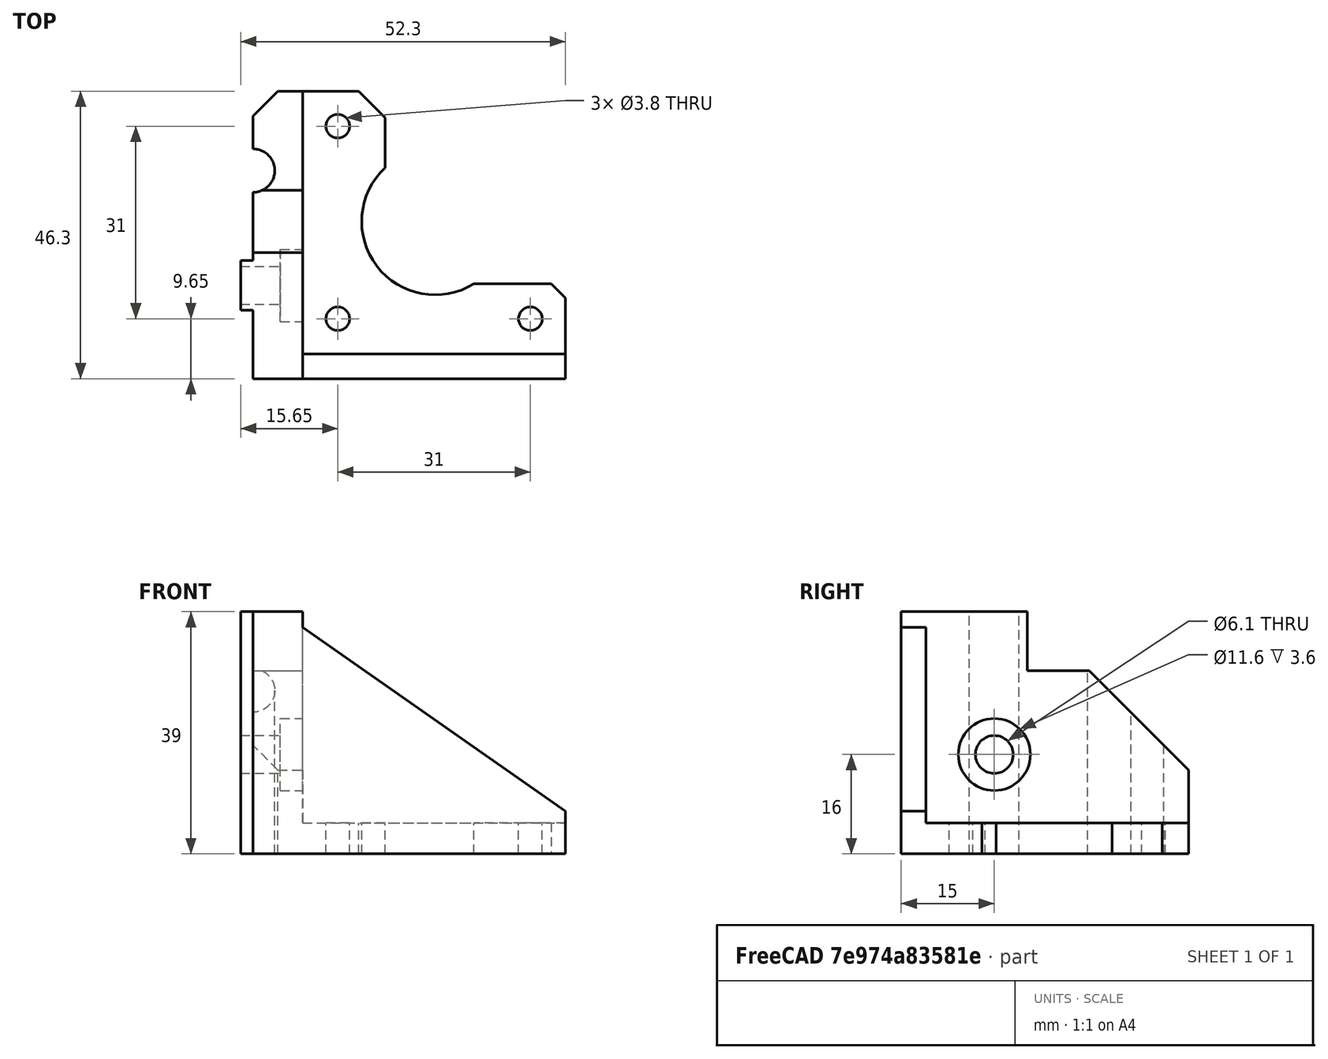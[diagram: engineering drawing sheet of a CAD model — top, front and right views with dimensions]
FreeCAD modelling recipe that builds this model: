
FCSTD DOCUMENT  (FreeCAD 0.19R)
Label: y-motor
License: All rights reserved
LicenseURL: http://en.wikipedia.org/wiki/All_rights_reserved
objects: Part::Box×12, Part::Cylinder×7, Part::MultiFuse×3, Part::Cut×2, Part::Fuse×2
note: 26 computed .brp shape members not serialized (recipe doc carries the construction recipe); baked Part::Feature solids carry a one-line shape summary decoded from their .brp

FEATURE [Part::Box] cube
  AttacherType = Attacher::AttachEngine3D
  Height = 39
  Length = 50.3
  Width = 46.3
FEATURE [Part::Box] cube001
  AttacherType = Attacher::AttachEngine3D
  Height = 60
  Length = 60
  Placement = pos=(8,4,5) rot=(0,0,1;0rad)
  Width = 60
FEATURE [Part::Cut] difference
  Base = -> cube
  Tool = -> cube001
FEATURE [Part::Box] cube002
  AttacherType = Attacher::AttachEngine3D
  Height = 39
  Length = 4
  Placement = pos=(-2,11,0) rot=(0,0,1;0rad)
  Width = 8
FEATURE [Part::Fuse] Group
  Base = -> difference
  Tool = -> cube002
FEATURE [Part::Box] cube003
  AttacherType = Attacher::AttachEngine3D
  Height = 40
  Length = 10
  Placement = pos=(8,5,36.5) rot=(-0.287968,0.287968,-0.913318;1.66134rad)
  Width = 70
FEATURE [Part::Box] cube004
  AttacherType = Attacher::AttachEngine3D
  Height = 40
  Length = 10
  Placement = pos=(8,5,36.5) rot=(0,0,-1;1.5708rad)
  Width = 70
FEATURE [Part::Box] cube005
  AttacherType = Attacher::AttachEngine3D
  Height = 10
  Length = 40
  Placement = pos=(21.3,17.3,-0.1) rot=(0,0,1;0rad)
  Width = 40
FEATURE [Part::Box] cube006
  AttacherType = Attacher::AttachEngine3D
  Height = 10
  Length = 15
  Placement = pos=(34.3,15.3,-0.1) rot=(0,0,1;0rad)
  Width = 15
FEATURE [Part::Box] cube007
  AttacherType = Attacher::AttachEngine3D
  Height = 10
  Length = 10
  Placement = pos=(50.3,13,-0.1) rot=(0,0,1;0.785398rad)
  Width = 10
FEATURE [Part::Box] cube008
  AttacherType = Attacher::AttachEngine3D
  Height = 10
  Length = 10
  Placement = pos=(17,46.3,-0.1) rot=(0,0,-1;0.785398rad)
  Width = 10
FEATURE [Part::Box] cube009
  AttacherType = Attacher::AttachEngine3D
  Height = 10
  Length = 10
  Placement = pos=(-0.1,20.3,29.5) rot=(0,0,1;0rad)
  Width = 20
FEATURE [Part::Box] cube010
  AttacherType = Attacher::AttachEngine3D
  Height = 40
  Length = 10
  Placement = pos=(-0.1,30.3,29.5) rot=(-1,0,0;0.785398rad)
  Width = 40
FEATURE [Part::Box] cube011
  AttacherType = Attacher::AttachEngine3D
  Height = 39
  Length = 10
  Placement = pos=(0,42.3,-0.1) rot=(0,0,1;0.785398rad)
  Width = 10
FEATURE [Part::Cylinder] cylinder
  Angle = 360
  AttacherType = Attacher::AttachEngine3D
  Height = 39
  Placement = pos=(0,33.5,-0.1) rot=(0,0,1;0rad)
  Radius = 3.5
FEATURE [Part::MultiFuse] Group001
  Shapes = -> [cube003,cube004,cube005,cube006,cube007,cube008,cube009,cube010,cube011,cylinder]
FEATURE [Part::Cylinder] cylinder001
  Angle = 360
  AttacherType = Attacher::AttachEngine3D
  Height = 10
  Placement = pos=(4.4,15,16) rot=(0,1,0;1.5708rad)
  Radius = 5.8
FEATURE [Part::Cylinder] cylinder002
  Angle = 360
  AttacherType = Attacher::AttachEngine3D
  Height = 10
  Placement = pos=(-3,15,16) rot=(0,1,0;1.5708rad)
  Radius = 3.05
FEATURE [Part::Cylinder] cylinder003
  Angle = 360
  AttacherType = Attacher::AttachEngine3D
  Height = 20
  Placement = pos=(0,0,-0.1) rot=(0,0,1;0rad)
  Radius = 1.9
FEATURE [Part::Cylinder] cylinder004
  Angle = 360
  AttacherType = Attacher::AttachEngine3D
  Height = 20
  Placement = pos=(31,0,-0.1) rot=(0,0,1;0rad)
  Radius = 1.9
FEATURE [Part::Cylinder] cylinder005
  Angle = 360
  AttacherType = Attacher::AttachEngine3D
  Height = 20
  Placement = pos=(0,31,-0.1) rot=(0,0,1;0rad)
  Radius = 1.9
FEATURE [Part::MultiFuse] Matrix_Union
  Placement = pos=(13.65,9.65,-0.1) rot=(0,0,1;0rad)
  Shapes = -> [cylinder003,cylinder004,cylinder005]
FEATURE [Part::Cylinder] cylinder006
  Angle = 360
  AttacherType = Attacher::AttachEngine3D
  Height = 10
  Placement = pos=(29.3,25.3,-0.1) rot=(0,0,1;0rad)
  Radius = 11.8
FEATURE [Part::MultiFuse] Group002
  Shapes = -> [cylinder001,cylinder002,Matrix_Union,cylinder006]
FEATURE [Part::Fuse] union
  Base = -> Group001
  Tool = -> Group002
FEATURE [Part::Cut] difference001
  Base = -> Group
  Refine = true
  Tool = -> union
